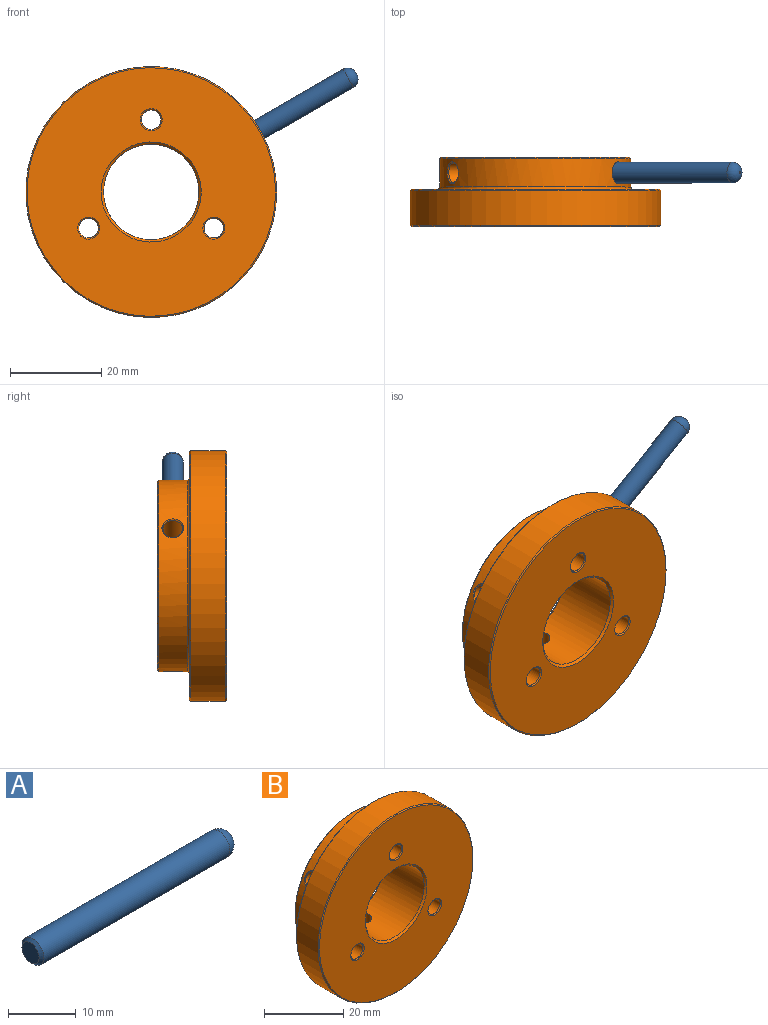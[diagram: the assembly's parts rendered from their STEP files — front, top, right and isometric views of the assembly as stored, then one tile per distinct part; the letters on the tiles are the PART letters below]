
ASSEMBLY  parts=2 mates=1
PART A: 5 faces, bbox 41.3x4.6x4.6 mm
  f0: cylinder r=2.29mm len=38.74mm, axis (-1,0,0), area 556.4mm2, adj f3,f4
  f1: plane 0.51x0.51mm, normal (1,0,0), area 0.2mm2, adj f3
  f2: plane 3.56x3.56mm, normal (-1,0,0), area 9.9mm2, adj f4
  f3: torus R=0.25mm, axis (1,0,0), area 31mm2, adj f0,f1
  f4: cone r=2.29mm half-angle=45deg, axis (1,0,0), area 9.2mm2, adj f0,f2
PART B: 27 faces, bbox 55.1x15.2x55.1 mm
  f0: cylinder r=27.55mm len=55.1mm, axis (0,-1,0), area 1323.4mm2, adj f12,f13
  f1: plane 54.59x54.59mm, normal (0,1,0), area 884.9mm2, adj f13,f15
  f2: plane 54.59x54.59mm, normal (0,-1,0), area 1906.7mm2, adj f12,f17,f21,f22,f23
  f3: cylinder r=21.02mm len=42.04mm, axis (0,-1,0), area 770.3mm2, adj f14,f15,f24,f25,f26
  f4: plane 41.53x41.53mm, normal (0,1,0), area 920.5mm2, adj f14,f16,f18,f19,f20
  f5: cylinder r=2.16mm len=14.66mm, axis (0,-1,0), area 198.8mm2, adj f18,f22
  f6: cylinder r=2.16mm len=14.66mm, axis (0,-1,0), area 198.8mm2, adj f19,f21
  f7: cylinder r=2.16mm len=14.66mm, axis (0,-1,0), area 198.8mm2, adj f20,f23
  f8: cylinder r=10.48mm len=20.96mm, axis (0,-1,0), area 887.3mm2, adj f9,f10,f11,f16,f17
  f9: cylinder r=2.16mm len=11.17mm, axis (0.87,0,-0.5), area 141.1mm2, adj f8,f24
  f10: cylinder r=2.16mm len=11.17mm, axis (-0.87,0,-0.5), area 141.1mm2, adj f8,f26
  f11: cylinder r=2.16mm len=10.31mm, axis (0,0,1), area 139.9mm2, adj f8,f25
  f12: cone r=27.3mm half-angle=45deg, axis (0,1,0), area 61.9mm2, adj f0,f2
  f13: cone r=27.55mm half-angle=45deg, axis (0,-1,0), area 61.9mm2, adj f0,f1
  f14: cone r=20.76mm half-angle=45deg, axis (0,-1,0), area 47.2mm2, adj f3,f4
  f15: torus R=21.53mm, axis (0,-1,0), area 106.3mm2, adj f1,f3
  f16: cone r=10.99mm half-angle=45deg, axis (0,1,0), area 48.4mm2, adj f4,f8
  f17: cone r=10.48mm half-angle=45deg, axis (0,-1,0), area 48.4mm2, adj f2,f8
  f18: cone r=2.41mm half-angle=45deg, axis (0,1,0), area 5.2mm2, adj f4,f5
  f19: cone r=2.41mm half-angle=45deg, axis (0,1,0), area 5.2mm2, adj f4,f6
  f20: cone r=2.41mm half-angle=45deg, axis (0,1,0), area 5.2mm2, adj f4,f7
  f21: cone r=2.16mm half-angle=45deg, axis (0,-1,0), area 5.2mm2, adj f2,f6
  f22: cone r=2.16mm half-angle=45deg, axis (0,-1,0), area 5.2mm2, adj f2,f5
  f23: cone r=2.16mm half-angle=45deg, axis (0,-1,0), area 5.2mm2, adj f2,f7
  f24: bspline ~4.77x4.18mm, area 4.8mm2, adj f3,f9
  f25: bspline ~4.83x4.78mm, area 4.8mm2, adj f3,f11
  f26: bspline ~4.77x4.18mm, area 4.8mm2, adj f3,f10
PLACE A rot(axis=(0,-1,0),30deg) t=(13.85,-10.66,25.57)mm
PLACE B t=(-13.29,-22.47,9.91)mm
MATE fastened A.f0 <-> B.f10  axis (-0.87,0,-0.5) through (-4.03,-10.66,15.25)mm
